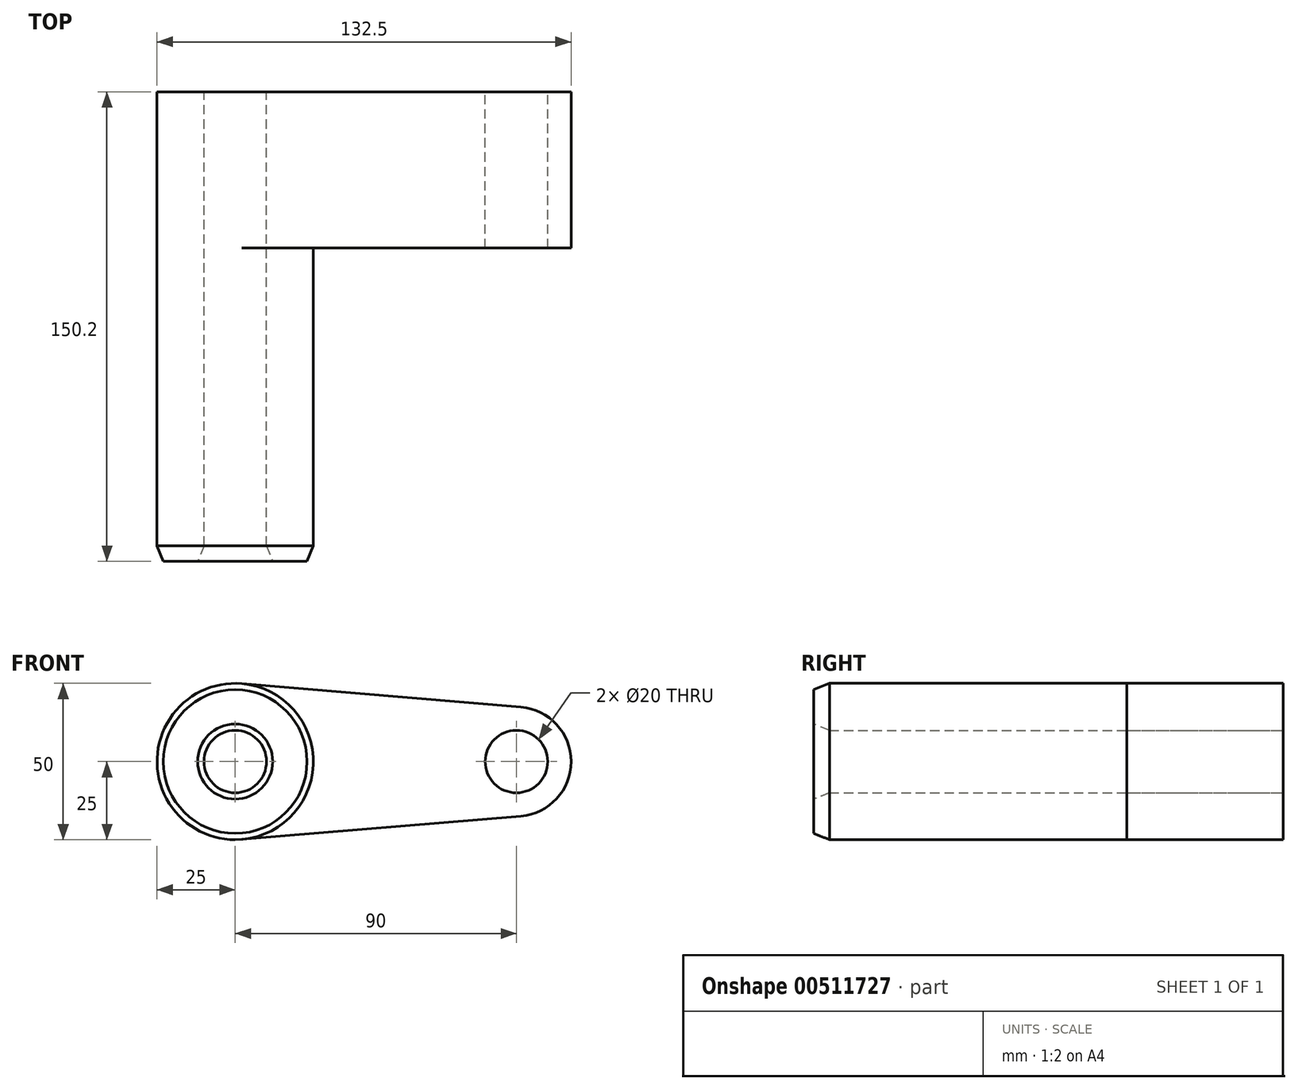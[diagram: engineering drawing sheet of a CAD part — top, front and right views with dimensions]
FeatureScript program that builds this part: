
annotation { "Feature Type Name" : "Feature", "Feature Type Description" : "" }
export const myFeature = defineFeature(function(context is Context, id is Id, definition is map)
    precondition{}
    {
        {
            var Q0;
            Q0=qCreatedBy(makeId("Front.planeOp"),FACE);
            var sketch = newSketch(context, id + "F0", { "sketchPlane" : qUnion([Q0])});
            skCircle(sketch, "E0", {"center": v(0, 0) * mm, "radius": 25 * mm});
            skCircle(sketch, "E1", {"center": v(90, 0) * mm, "radius": 17.5 * mm});
            skLineSegment(sketch, "E2", {"start": v(2.08, 24.91) * mm, "end": v(91.46, 17.44) * mm});
            skLineSegment(sketch, "E3", {"start": v(2.08, -24.91) * mm, "end": v(91.46, -17.44) * mm});
            skCircle(sketch, "E4", {"center": v(0, 0) * mm, "radius": 10 * mm});
            skCircle(sketch, "E5", {"center": v(90, 0) * mm, "radius": 10 * mm});
            skSolve(sketch);
        }
        {
            var Q0;
            Q0=qSketchRegion(id+"F0",true);
            extrude(context, id + "F1", {"entities" : qUnion([Q0]), "depth" : 50 * mm});
        }
        {
            var Q0;
            Q0=makeQuery(id+"F0.imprint","IMPRINT",FACE,{"disambiguationData":[TD([[makeQuery(id+"F0.imprint","IMPRINT",EDGE,{"derivedFrom":sQuery(id+"F0.wireOp",EDGE,"E4")}),-1.0]])]});
            extrude(context, id + "F2", {"entities" : qUnion([Q0]), "operationType" : NewBodyOperationType.ADD, "endBound" : BoundingType.THROUGH_ALL, "depth" : 50 * mm});
        }
        {
            var Q0;
            Q0=makeQuery(id+"F2.opExtrude","CAP_FACE",FACE,{"disambiguationData":[OSD([sQuery(id+"F0.wireOp",EDGE,"E0"),sQuery(id+"F0.wireOp",EDGE,"E4")])],"isStart":false});
            chamfer(context, id + "F3", {"entities" : qUnion([Q0]), "chamferType" : ChamferType.TWO_OFFSETS, "width1" : 2 * mm, "oppositeDirection" : false, "width2" : 5 * mm, "tangentPropagation" : true});
        }
    });
